# Revit family: Вставка гибкая G прямоугольная
name_source: partatom
category: Арматура воздуховодов
units: mm (PartAtom-declared; Revit-internal decimal feet)

## family parameters
Всегда вертикально = Да
На основе рабочей плоскости = Нет
Общий = Нет
При загрузке вырезать с полостями = Нет
Размер круглого соединителя = Использовать диаметр
Тип детали = Вставляется

## types (8) — shared parameters
ADSK_Единица измерения = шт.
ADSK_Завод-изготовитель = Naveka
ADSK_Наименование = Вставка гибкая прямоугольная
Материал = RAL 0000 Серый металл
zero-valued in all types: ADSK_Масса

## per-type parameters (varying)
| type | ADSK_Марка | B | H | w |
| Вставка гибкая G-4020 | G-4020 | 400 мм | 200 мм | 20 мм |
| Вставка гибкая G-5025 | G-5025 | 500 мм | 250 мм | 20 мм |
| Вставка гибкая G-5030 | G-5030 | 500 мм | 300 мм | 20 мм |
| Вставка гибкая G-6030 | G-6030 | 600 мм | 300 мм | 20 мм |
| Вставка гибкая G-6035 | G-6035 | 600 мм | 350 мм | 20 мм |
| Вставка гибкая G-7040 | G-7040 | 700 мм | 400 мм | 30 мм |
| Вставка гибкая G-8050 | G-8050 | 800 мм | 500 мм | 30 мм |
| Вставка гибкая G-10050 | G-10050 | 1000 мм | 500 мм | 30 мм |
